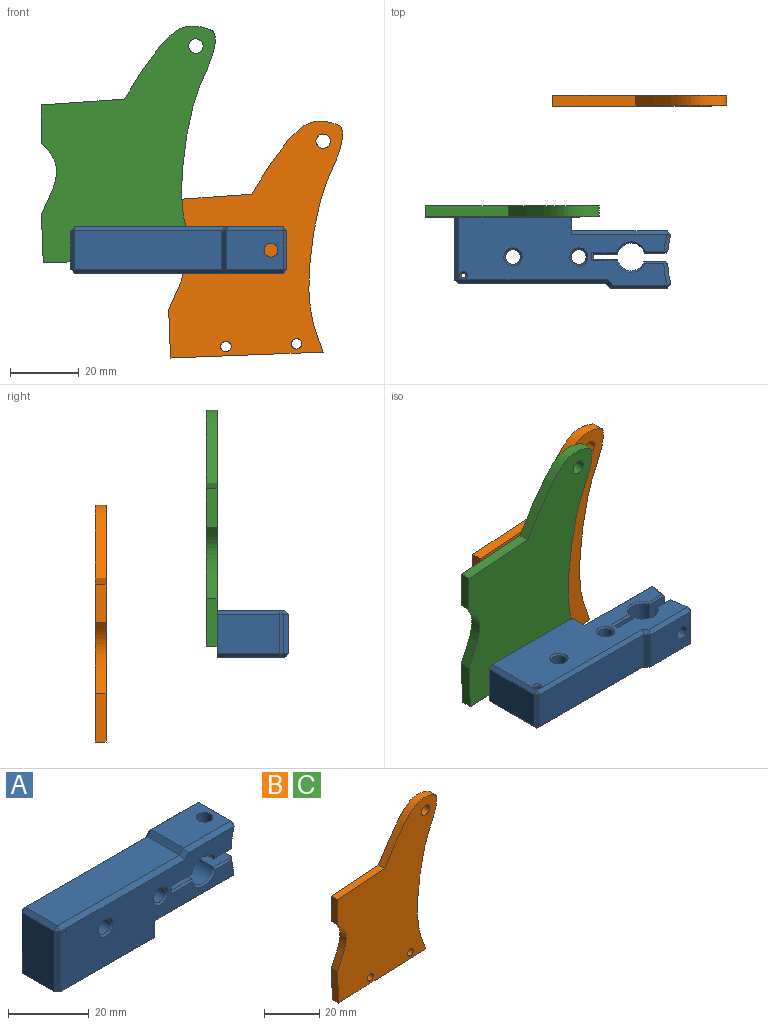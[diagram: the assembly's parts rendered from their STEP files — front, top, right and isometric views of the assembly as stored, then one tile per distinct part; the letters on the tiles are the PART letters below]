
ASSEMBLY  parts=3 mates=1
PART A: 76 faces, bbox 63.1x13.9x21.1 mm
  f0: plane 13.59x5.08mm, normal (1,0,0), area 54.8mm2, adj f1,f17,f19,f20,f45,f50
  f1: plane 27.74x11.3mm, normal (0,0,-1), area 293.2mm2, adj f0,f27,f45,f48,f50
  f2: extruded ~11.3x4.66mm, area 53.6mm2, adj f44,f47,f48,f62
  f3: plane 12.57x6.33mm, normal (0,0,1), area 65.9mm2, adj f4,f26,f58,f60,f62,f64,f66
  f4: cylinder r=4.01mm len=12.57mm, axis (0,1,0), area 135.1mm2, adj f3,f5,f56,f68
  f5: plane 12.57x7mm, normal (0,0,1), area 88mm2, adj f4,f6,f54,f70
  f6: plane 12.57x1.41mm, normal (1,0,0), area 17.8mm2, adj f5,f7,f55,f72
  f7: plane 12.57x6.97mm, normal (0,0,-1), area 87.7mm2, adj f6,f8,f57,f73
  f8: cylinder r=4.01mm len=12.57mm, axis (0,1,0), area 132mm2, adj f7,f9,f59,f71
  f9: plane 12.57x6.4mm, normal (0,0,-1), area 66.8mm2, adj f8,f25,f61,f63,f65,f67,f69
  f10: extruded ~11.3x5.94mm, area 68.1mm2, adj f28,f31,f32,f65
  f11: plane 16.55x11.3mm, normal (0,0,1), area 174.1mm2, adj f12,f25,f30,f31,f37
  f12: plane 11.3x1.47mm, normal (-0.75,0,0.66), area 22.3mm2, adj f11,f13,f33,f39
  f13: plane 42.86x11.3mm, normal (0,0,1), area 484.5mm2, adj f12,f36,f40,f41
  f14: plane 18.31x11.3mm, normal (-1,0,0), area 207mm2, adj f17,f35,f40,f43
  f15: cylinder r=2.15mm len=12.57mm, axis (0,1,0), area 169.6mm2, adj f52,f74
  f16: cylinder r=2.15mm len=12.57mm, axis (0,1,0), area 169.6mm2, adj f53,f75
  f17: plane 34.11x13.59mm, normal (0,0,-1), area 436.6mm2, adj f0,f14,f19,f20,f22,f24,f35,f43
  f18: cylinder r=0.66mm len=13.08mm, axis (0,1,0), area 54.6mm2, adj f19,f51
  f19: plane 60.9x19.96mm, normal (0,-1,0), area 841.4mm2, adj f0,f17,f18,f32,f37,f39,f41,f43
  f20: plane 60.9x19.96mm, normal (0,1,0), area 837.8mm2, adj f0,f17,f28,f30,f33,f35,f36,f44
  f21: plane 4.04x4.04mm, normal (0,0,-1), area 12.8mm2, adj f22
  f22: cylinder r=2.02mm len=14.41mm, axis (0,0,1), area 182.8mm2, adj f17,f21
  f23: plane 4.04x4.04mm, normal (0,0,-1), area 12.8mm2, adj f24
  f24: cylinder r=2.02mm len=14.41mm, axis (0,0,1), area 182.8mm2, adj f17,f23
  f25: cylinder r=2.03mm len=7.88mm, axis (0,0,-1), area 100.7mm2, adj f9,f11
  f26: cylinder r=2.03mm len=6.1mm, axis (0,0,-1), area 77.8mm2, adj f3,f27
  f27: cone r=2.03mm half-angle=45deg, axis (0,0,-1), area 10.3mm2, adj f1,f26
  f28: bspline ~6.3x2.08mm, area 10mm2, adj f10,f20,f29,f67
  f29: plane 1.46x1.14mm, normal (0.69,0.51,0.51), area 1.2mm2, adj f28,f30,f31
  f30: plane 16.55x1.14mm, normal (0,0.71,0.71), area 26.3mm2, adj f11,f20,f29,f33
  f31: plane 11.3x1.46mm, normal (0.8,0,0.6), area 20.7mm2, adj f10,f11,f29,f34
  f32: bspline ~6.3x2.08mm, area 10mm2, adj f10,f19,f34,f63
  f33: plane 2.62x1.82mm, normal (-0.53,0.71,0.47), area 3.2mm2, adj f12,f20,f30,f36
  f34: plane 1.46x1.14mm, normal (0.69,-0.51,0.51), area 1.2mm2, adj f31,f32,f37
  f35: plane 18.31x1.14mm, normal (-0.71,0.71,0), area 29.6mm2, adj f14,f17,f20,f38
  f36: plane 43.38x1.14mm, normal (0,0.71,0.71), area 69.7mm2, adj f13,f20,f33,f38
  f37: plane 16.55x1.14mm, normal (0,-0.71,0.71), area 26.3mm2, adj f11,f19,f34,f39
  f38: plane 1.14x1.14mm, normal (-0.58,0.58,0.58), area 1.1mm2, adj f35,f36,f40
  f39: plane 2.62x1.82mm, normal (-0.53,-0.71,0.47), area 3.2mm2, adj f12,f19,f37,f41
  f40: plane 11.3x1.14mm, normal (-0.71,0,0.71), area 18.3mm2, adj f13,f14,f38,f42
  f41: plane 43.38x1.14mm, normal (0,-0.71,0.71), area 69.7mm2, adj f13,f19,f39,f42
  f42: plane 1.14x1.14mm, normal (-0.58,-0.58,0.58), area 1.1mm2, adj f40,f41,f43
  f43: plane 18.31x1.14mm, normal (-0.71,-0.71,0), area 29.6mm2, adj f14,f17,f19,f42
  f44: bspline ~5.06x2.02mm, area 7.9mm2, adj f2,f20,f46,f64,f66
  f45: plane 27.74x1.14mm, normal (0,0.71,-0.71), area 44.8mm2, adj f0,f1,f20,f46
  f46: plane 1.48x1.14mm, normal (0.69,0.51,-0.51), area 1.2mm2, adj f44,f45,f48
  f47: bspline ~5.06x2.02mm, area 7.9mm2, adj f2,f19,f49,f58,f60
  f48: plane 11.3x1.48mm, normal (0.8,0,-0.59), area 20.8mm2, adj f1,f2,f46,f49
  f49: plane 1.48x1.14mm, normal (0.69,-0.51,-0.51), area 1.2mm2, adj f47,f48,f50
  f50: plane 27.74x1.14mm, normal (0,-0.71,-0.71), area 44.8mm2, adj f0,f1,f19,f49
  f51: cone r=1.17mm half-angle=45deg, axis (0,1,0), area 4.1mm2, adj f18,f20
  f52: cone r=2.65mm half-angle=45deg, axis (0,1,0), area 10.8mm2, adj f15,f20
  f53: cone r=2.65mm half-angle=45deg, axis (0,1,0), area 10.8mm2, adj f16,f20
  f54: plane 7.52x0.53mm, normal (0,-0.71,0.71), area 5.1mm2, adj f5,f19,f55,f56
  f55: plane 2.43x0.51mm, normal (0.71,-0.71,0), area 1.4mm2, adj f6,f19,f54,f57
  f56: cone r=4.01mm half-angle=45deg, axis (0,-1,0), area 7.9mm2, adj f4,f19,f54,f58
  f57: plane 7.5x0.53mm, normal (0,-0.71,-0.71), area 5mm2, adj f7,f19,f55,f59
  f58: plane 5.74x0.53mm, normal (0,-0.71,0.71), area 3.9mm2, adj f3,f19,f47,f56,f60
  f59: cone r=4.01mm half-angle=45deg, axis (0,-1,0), area 7.7mm2, adj f8,f19,f57,f61
  f60: bspline ~1.49x1.49mm, area 1mm2, adj f3,f47,f58,f62
  f61: plane 5.79x0.53mm, normal (0,-0.71,-0.71), area 3.9mm2, adj f9,f19,f59,f63
  f62: plane 11.31x0.52mm, normal (0.68,0,0.73), area 7.7mm2, adj f2,f3,f60,f64
  f63: bspline ~1.63x1.63mm, area 1mm2, adj f9,f32,f61,f65
  f64: bspline ~1.49x1.49mm, area 1mm2, adj f3,f44,f62,f66
  f65: plane 11.31x0.52mm, normal (0.69,0,-0.72), area 7.8mm2, adj f9,f10,f63,f67
  f66: plane 5.74x0.53mm, normal (0,0.71,0.71), area 3.9mm2, adj f3,f20,f44,f64,f68
  f67: bspline ~1.63x1.63mm, area 1mm2, adj f9,f28,f65,f69
  f68: cone r=4.52mm half-angle=45deg, axis (0,1,0), area 7.9mm2, adj f4,f20,f66,f70
  f69: plane 5.79x0.53mm, normal (0,0.71,-0.71), area 3.9mm2, adj f9,f20,f67,f71
  f70: plane 7.52x0.53mm, normal (0,0.71,0.71), area 5.1mm2, adj f5,f20,f68,f72
  f71: cone r=4.52mm half-angle=45deg, axis (0,1,0), area 7.7mm2, adj f8,f20,f69,f73
  f72: plane 2.43x0.51mm, normal (0.71,0.71,0), area 1.4mm2, adj f6,f20,f70,f73
  f73: plane 7.5x0.53mm, normal (0,0.71,-0.71), area 5mm2, adj f7,f20,f71,f72
  f74: cone r=2.15mm half-angle=45deg, axis (0,-1,0), area 10.8mm2, adj f15,f19
  f75: cone r=2.15mm half-angle=45deg, axis (0,-1,0), area 10.8mm2, adj f16,f19
PART B: 11 faces, bbox 51.3x3.2x69.7 mm
  f0: plane 44.47x3.18mm, normal (0.04,0,-1), area 141.3mm2, adj f1,f8,f9,f10
  f1: extruded ~67.32x26.53mm, area 331.2mm2, adj f0,f2,f9,f10
  f2: plane 24.15x3.18mm, normal (-0.07,0,1), area 76.9mm2, adj f1,f3,f9,f10
  f3: plane 11.1x3.18mm, normal (-1,0,0), area 35.2mm2, adj f2,f4,f9,f10
  f4: extruded ~20.83x4.41mm, area 73.2mm2, adj f3,f8,f9,f10
  f5: cylinder r=2.1mm len=4.19mm, axis (0,1,0), area 41.8mm2, adj f9,f10
  f6: cylinder r=1.52mm len=3.18mm, axis (0,1,0), area 30.4mm2, adj f9,f10
  f7: cylinder r=1.52mm len=3.18mm, axis (0,1,0), area 30.4mm2, adj f9,f10
  f8: plane 14.09x3.18mm, normal (-1,0,-0.04), area 44.8mm2, adj f0,f4,f9,f10
  f9: plane 69.7x51.34mm, normal (0,-1,0), area 2229.4mm2, adj f0,f1,f2,f3,f4,f5,f6,f7
  f10: plane 69.7x51.34mm, normal (0,1,0), area 2229.4mm2, adj f0,f1,f2,f3,f4,f5,f6,f7
PART C: same geometry as B
PLACE A rot(axis=(1,0,0),90deg) t=(21.23,-32.93,-11.28)mm
PLACE B t=(62.32,16.99,-54.97)mm
PLACE C t=(25.24,-15.35,-27.26)mm
MATE fastened A.f22 <-> C.f7  axis (0,1,0) through (17.48,-18.52,-17.68)mm
